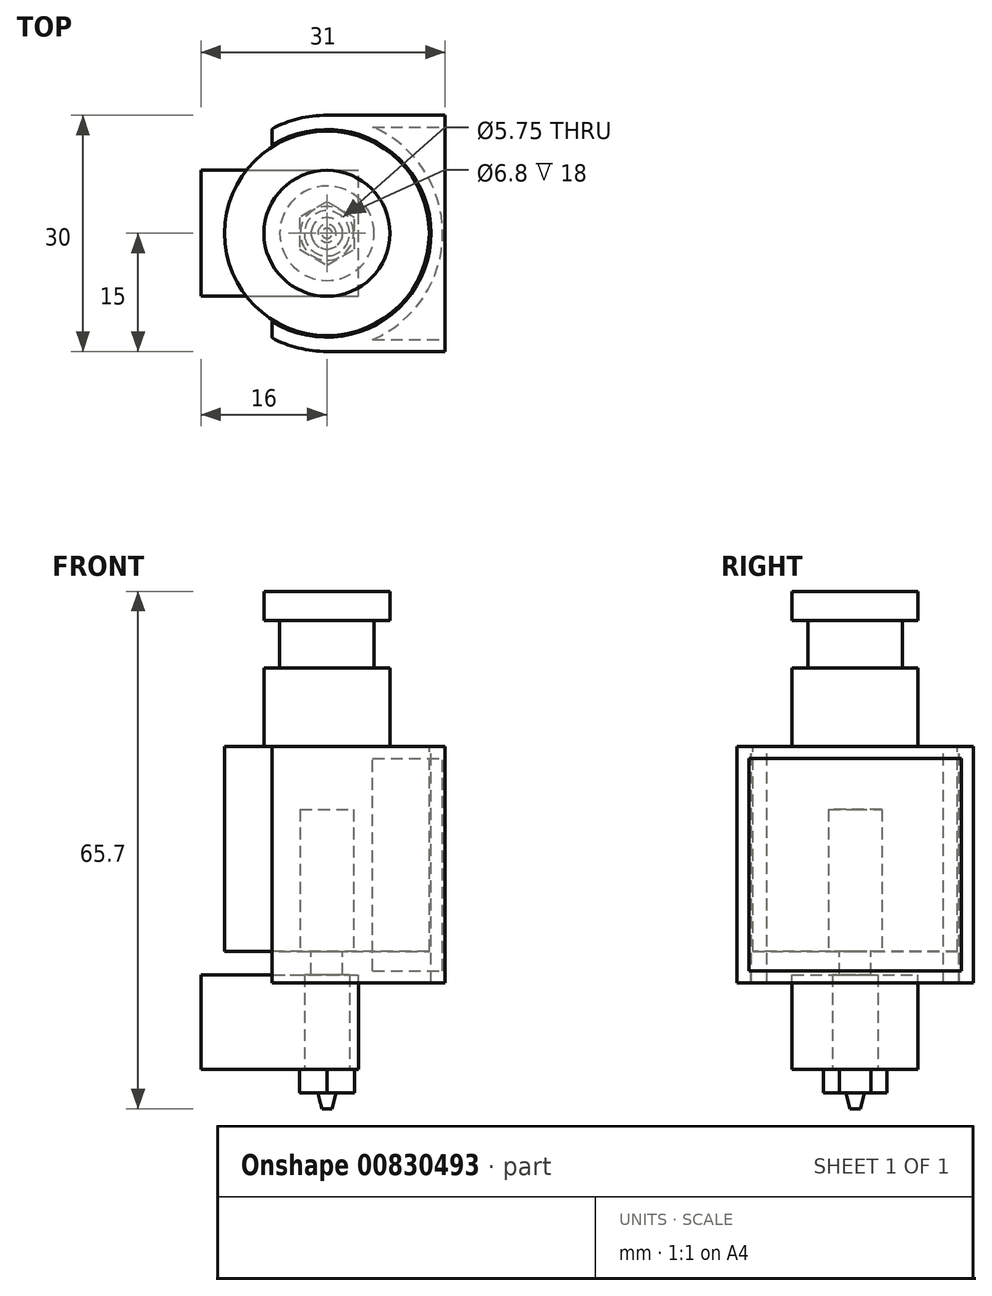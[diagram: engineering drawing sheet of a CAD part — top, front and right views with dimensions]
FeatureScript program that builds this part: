
annotation { "Feature Type Name" : "Feature", "Feature Type Description" : "" }
export const myFeature = defineFeature(function(context is Context, id is Id, definition is map)
    precondition{}
    {
        {
            var Q0;
            Q0=qCreatedBy(makeId("Top.planeOp"),FACE);
            var sketch = newSketch(context, id + "F0", { "sketchPlane" : qUnion([Q0])});
            skCircle(sketch, "E0", {"center": v(0, 0) * mm, "radius": 8 * mm});
            skSolve(sketch);
        }
        {
            var Q0;
            Q0=qSketchRegion(id+"F0",true);
            extrude(context, id + "F1", {"entities" : qUnion([Q0]), "depth" : 3.7 * mm});
        }
        {
            var Q0;
            Q0=makeQuery(id+"F1.opExtrude","CAP_FACE",FACE,{"disambiguationData":[OSD([sQuery(id+"F0.wireOp",EDGE,"E0")])],"isStart":true});
            var sketch = newSketch(context, id + "F2", { "sketchPlane" : qUnion([Q0])});
            skCircle(sketch, "E1", {"center": v(0, 0) * mm, "radius": 6 * mm});
            skSolve(sketch);
        }
        {
            var Q0;
            Q0=qSketchRegion(id+"F2",true);
            extrude(context, id + "F3", {"entities" : qUnion([Q0]), "operationType" : NewBodyOperationType.ADD, "depth" : 6 * mm});
        }
        {
            var Q0;
            Q0=makeQuery(id+"F3.opExtrude","CAP_FACE",FACE,{"disambiguationData":[OSD([sQuery(id+"F2.wireOp",EDGE,"E1")])],"isStart":false});
            var sketch = newSketch(context, id + "F4", { "sketchPlane" : qUnion([Q0])});
            skCircle(sketch, "E2", {"center": v(0, 0) * mm, "radius": 8 * mm});
            skSolve(sketch);
        }
        {
            var Q0;
            Q0=qSketchRegion(id+"F4",true);
            extrude(context, id + "F5", {"entities" : qUnion([Q0]), "operationType" : NewBodyOperationType.ADD, "depth" : (3 + 7) * mm, "offsetDistance" : 25 * mm});
        }
        {
            var Q0;
            Q0=makeQuery(id+"F5.opExtrude","CAP_FACE",FACE,{"disambiguationData":[OSD([sQuery(id+"F4.wireOp",EDGE,"E2")])],"isStart":false});
            var sketch = newSketch(context, id + "F6", { "sketchPlane" : qUnion([Q0])});
            skCircle(sketch, "E3", {"center": v(0, 0) * mm, "radius": 13 * mm});
            skSolve(sketch);
        }
        {
            var Q0;
            Q0=qSketchRegion(id+"F6",true);
            extrude(context, id + "F7", {"entities" : qUnion([Q0]), "operationType" : NewBodyOperationType.ADD, "depth" : 26 * mm, "offsetDistance" : 25 * mm});
        }
        {
            var Q0;
            Q0=makeQuery(id+"F7.opExtrude","CAP_FACE",FACE,{"disambiguationData":[OSD([sQuery(id+"F6.wireOp",EDGE,"E3")])],"isStart":false});
            var sketch = newSketch(context, id + "F8", { "sketchPlane" : qUnion([Q0])});
            skCircle(sketch, "E4", {"center": v(0, 0) * mm, "radius": 3.4 * mm});
            skSolve(sketch);
        }
        {
            var Q0;
            Q0=qSketchRegion(id+"F8",true);
            extrude(context, id + "F9", {"entities" : qUnion([Q0]), "operationType" : NewBodyOperationType.REMOVE, "oppositeDirection" : true, "depth" : 18 * mm, "offsetDistance" : 25 * mm});
        }
        {
            var Q0;
            Q0=makeQuery(id+"F7.opExtrude","CAP_FACE",FACE,{"disambiguationData":[OSD([sQuery(id+"F6.wireOp",EDGE,"E3")])],"isStart":false});
            var sketch = newSketch(context, id + "F10", { "sketchPlane" : qUnion([Q0])});
            skCircle(sketch, "E5", {"center": v(0, 0) * mm, "radius": 3.4 * mm});
            skSolve(sketch);
        }
        {
            var Q0;
            Q0=qSketchRegion(id+"F10",true);
            extrude(context, id + "F11", {"entities" : qUnion([Q0]), "oppositeDirection" : true, "depth" : 18 * mm, "offsetDistance" : 25 * mm});
        }
        {
            var Q0;
            Q0=makeQuery(id+"F11.opExtrude","CAP_FACE",FACE,{"disambiguationData":[OSD([sQuery(id+"F10.wireOp",EDGE,"E5")])],"isStart":true});
            var sketch = newSketch(context, id + "F12", { "sketchPlane" : qUnion([Q0])});
            skCircle(sketch, "E6", {"center": v(0, 0) * mm, "radius": 2 * mm});
            skSolve(sketch);
        }
        {
            var Q0;
            Q0=qSketchRegion(id+"F12",true);
            extrude(context, id + "F13", {"entities" : qUnion([Q0]), "operationType" : NewBodyOperationType.ADD, "depth" : 3 * mm, "offsetDistance" : 25 * mm});
        }
        {
            var Q0;
            Q0=makeQuery(id+"F13.opExtrude","CAP_FACE",FACE,{"disambiguationData":[OSD([sQuery(id+"F12.wireOp",EDGE,"E6")])],"isStart":false});
            var sketch = newSketch(context, id + "F14", { "sketchPlane" : qUnion([Q0])});
            skCircle(sketch, "E7", {"center": v(0, 0) * mm, "radius": 2.88 * mm});
            skSolve(sketch);
        }
        {
            var Q0;
            Q0=qSketchRegion(id+"F14",true);
            extrude(context, id + "F15", {"entities" : qUnion([Q0]), "operationType" : NewBodyOperationType.ADD, "depth" : 5 * mm, "offsetDistance" : 25 * mm});
        }
        {
            var Q0;
            Q0=makeQuery(id+"F15.opExtrude","CAP_FACE",FACE,{"disambiguationData":[OSD([sQuery(id+"F14.wireOp",EDGE,"E7")])],"isStart":true});
            var sketch = newSketch(context, id + "F16", { "sketchPlane" : qUnion([Q0])});
            skLineSegment(sketch, "E8.bottom", {"start": v(-16, -8) * mm, "end": v(4, -8) * mm});
            skLineSegment(sketch, "E8.top", {"start": v(-16, 8) * mm, "end": v(4, 8) * mm});
            skLineSegment(sketch, "E8.left", {"start": v(-16, -8) * mm, "end": v(-16, 8) * mm});
            skLineSegment(sketch, "E8.right", {"start": v(4, -8) * mm, "end": v(4, 8) * mm});
            skLineSegment(sketch, "E9", {"start": v(-16, 0) * mm, "end": v(4, 0) * mm, "construction": true});
            skSolve(sketch);
        }
        {
            var Q0;
            Q0=qSketchRegion(id+"F16",true);
            extrude(context, id + "F17", {"entities" : qUnion([Q0]), "oppositeDirection" : true, "depth" : 12 * mm, "offsetDistance" : 25 * mm});
        }
        {
            var Q0;
            Q0=makeQuery(id+"F17.opExtrude","CAP_FACE",FACE,{"disambiguationData":[OSD([sQuery(id+"F16.wireOp",EDGE,"E8.bottom"),sQuery(id+"F16.wireOp",EDGE,"E8.top"),sQuery(id+"F16.wireOp",EDGE,"E8.left"),sQuery(id+"F16.wireOp",EDGE,"E8.right"),sQuery(id+"F16.wireOp",EDGE,"HFBCL504-6D1g-G369-yvVv-FWpguWhtGj3m")])],"isStart":false});
            var sketch = newSketch(context, id + "F18", { "sketchPlane" : qUnion([Q0])});
            skCircle(sketch, "E10", {"center": v(0, 0) * mm, "radius": 2.88 * mm});
            skSolve(sketch);
        }
        {
            var Q0;
            Q0=qSketchRegion(id+"F18",true);
            var Q1;
            Q1=makeQuery(id+"F17.opExtrude","CAP_FACE",FACE,{"disambiguationData":[OSD([sQuery(id+"F16.wireOp",EDGE,"E8.bottom"),sQuery(id+"F16.wireOp",EDGE,"E8.top"),sQuery(id+"F16.wireOp",EDGE,"E8.left"),sQuery(id+"F16.wireOp",EDGE,"E8.right")])],"isStart":true});
            extrude(context, id + "F19", {"entities" : qUnion([Q0]), "operationType" : NewBodyOperationType.REMOVE, "endBound" : BoundingType.UP_TO_SURFACE, "oppositeDirection" : true, "depth" : 25 * mm, "endBoundEntityFace" : qUnion([Q1]), "offsetDistance" : 25 * mm});
        }
        {
            var Q0;
            Q0=makeQuery(id+"F18.imprint","IMPRINT",FACE,{"disambiguationData":[TD([[makeQuery(id+"F18.imprint","IMPRINT",EDGE,{"derivedFrom":sQuery(id+"F18.wireOp",EDGE,"E10")}),-1.0]])]});
            var sketch = newSketch(context, id + "F20", { "sketchPlane" : qUnion([Q0])});
            skCircle(sketch, "E11.cCircle", {"center": v(0, 0) * mm, "radius": 3.5 * mm, "construction": true});
            skLineSegment(sketch, "E11.0", {"start": v(-3.5, -2.02) * mm, "end": v(-3.5, 2.02) * mm});
            skLineSegment(sketch, "E11.1", {"start": v(-3.5, 2.02) * mm, "end": v(0, 4.04) * mm});
            skLineSegment(sketch, "E11.2", {"start": v(0, 4.04) * mm, "end": v(3.5, 2.02) * mm});
            skLineSegment(sketch, "E11.3", {"start": v(3.5, 2.02) * mm, "end": v(3.5, -2.02) * mm});
            skLineSegment(sketch, "E11.4", {"start": v(3.5, -2.02) * mm, "end": v(0, -4.04) * mm});
            skLineSegment(sketch, "E11.5", {"start": v(0, -4.04) * mm, "end": v(-3.5, -2.02) * mm});
            skPoint(sketch, "E11.0.midPoint", {"position": v(-3.5, 0) * mm});
            skSolve(sketch);
        }
        {
            var Q0;
            Q0=qSketchRegion(id+"F20",true);
            extrude(context, id + "F21", {"entities" : qUnion([Q0]), "depth" : 3 * mm, "offsetDistance" : 25 * mm});
        }
        {
            var Q0;
            Q0=makeQuery(id+"F18.imprint","IMPRINT",FACE,{"disambiguationData":[TD([[makeQuery(id+"F18.imprint","IMPRINT",EDGE,{"derivedFrom":sQuery(id+"F18.wireOp",EDGE,"E10")}),-1.0]])]});
            var sketch = newSketch(context, id + "F22", { "sketchPlane" : qUnion([Q0])});
            skCircle(sketch, "E12", {"center": v(0, 0) * mm, "radius": 1.9 * mm});
            skSolve(sketch);
        }
        {
            var Q0;
            Q0=makeQuery(id+"F21.opExtrude","CAP_FACE",FACE,{"disambiguationData":[OSD([sQuery(id+"F20.wireOp",EDGE,"E11.0"),sQuery(id+"F20.wireOp",EDGE,"E11.1"),sQuery(id+"F20.wireOp",EDGE,"E11.2"),sQuery(id+"F20.wireOp",EDGE,"E11.3"),sQuery(id+"F20.wireOp",EDGE,"E11.4"),sQuery(id+"F20.wireOp",EDGE,"E11.5")])],"isStart":false});
            cPlane(context, id + "F23", {"entities" : qUnion([Q0]), "cplaneType" : CPlaneType.OFFSET, "offset" : 2 * mm, "width" : 150 * mm, "height" : 150 * mm});
        }
        {
            var Q0;
            Q0=qCreatedBy(id+"F23.planeOp",FACE);
            var sketch = newSketch(context, id + "F24", { "sketchPlane" : qUnion([Q0])});
            skCircle(sketch, "E13", {"center": v(0, 0) * mm, "radius": 0.65 * mm});
            skSolve(sketch);
        }
        {
            var Q1;
            Q1=qSketchRegion(id+"F22",true);
            var Q2;
            Q2=qSketchRegion(id+"F24",true);
            loft(context, id + "F25", {"operationType" : NewBodyOperationType.ADD, "sheetProfilesArray" : [{ "sheetProfileEntities" : qUnion([Q1]) }, { "sheetProfileEntities" : qUnion([Q2]) }]});
        }
        {
            var Q0;
            Q0=makeQuery(id+"F7.opExtrude","CAP_FACE",FACE,{"disambiguationData":[OSD([sQuery(id+"F6.wireOp",EDGE,"E3")])],"isStart":true});
            var sketch = newSketch(context, id + "F26", { "sketchPlane" : qUnion([Q0])});
            skArc(sketch, "E14.0", {"start": v(-7, -13.27) * mm, "mid": v(-3.6, -14.56) * mm, "end": v(0, -15) * mm});
            skLineSegment(sketch, "E15", {"start": v(-7, 13.27) * mm, "end": v(-7, 11.2) * mm});
            skCircle(sketch, "E16.0", {"center": v(0, 0) * mm, "radius": 13.2 * mm});
            skLineSegment(sketch, "E17.trimOffspring", {"start": v(-7, -11.2) * mm, "end": v(-7, -13.27) * mm});
            skLineSegment(sketch, "E18.bottom", {"start": v(0, 15) * mm, "end": v(15, 15) * mm});
            skLineSegment(sketch, "E18.top", {"start": v(0, -15) * mm, "end": v(15, -15) * mm});
            skLineSegment(sketch, "E18.right", {"start": v(15, 15) * mm, "end": v(15, -15) * mm});
            skArc(sketch, "E19.trimOffspring", {"start": v(0, 15) * mm, "mid": v(-3.6, 14.56) * mm, "end": v(-7, 13.27) * mm});
            skSolve(sketch);
        }
        {
            var Q0;
            Q0=makeQuery(id+"F26.imprint","IMPRINT",FACE,{"disambiguationData":[TD([[makeQuery(id+"F26.imprint","IMPRINT",EDGE,{"derivedFrom":sQuery(id+"F26.wireOp",EDGE,"E14.0")}),1.0]])]});
            extrude(context, id + "F27", {"entities" : qUnion([Q0]), "oppositeDirection" : true, "depth" : 30 * mm, "offsetDistance" : 25 * mm});
        }
        {
            var Q0;
            Q0=makeQuery(id+"F27.opExtrude","SWEPT_FACE",FACE,{"disambiguationData":[OSD([sQuery(id+"F26.wireOp",EDGE,"E18.right")])]});
            shell(context, id + "F28", {"entities" : qUnion([Q0]), "thickness" : 1.5 * mm});
        }
    });
